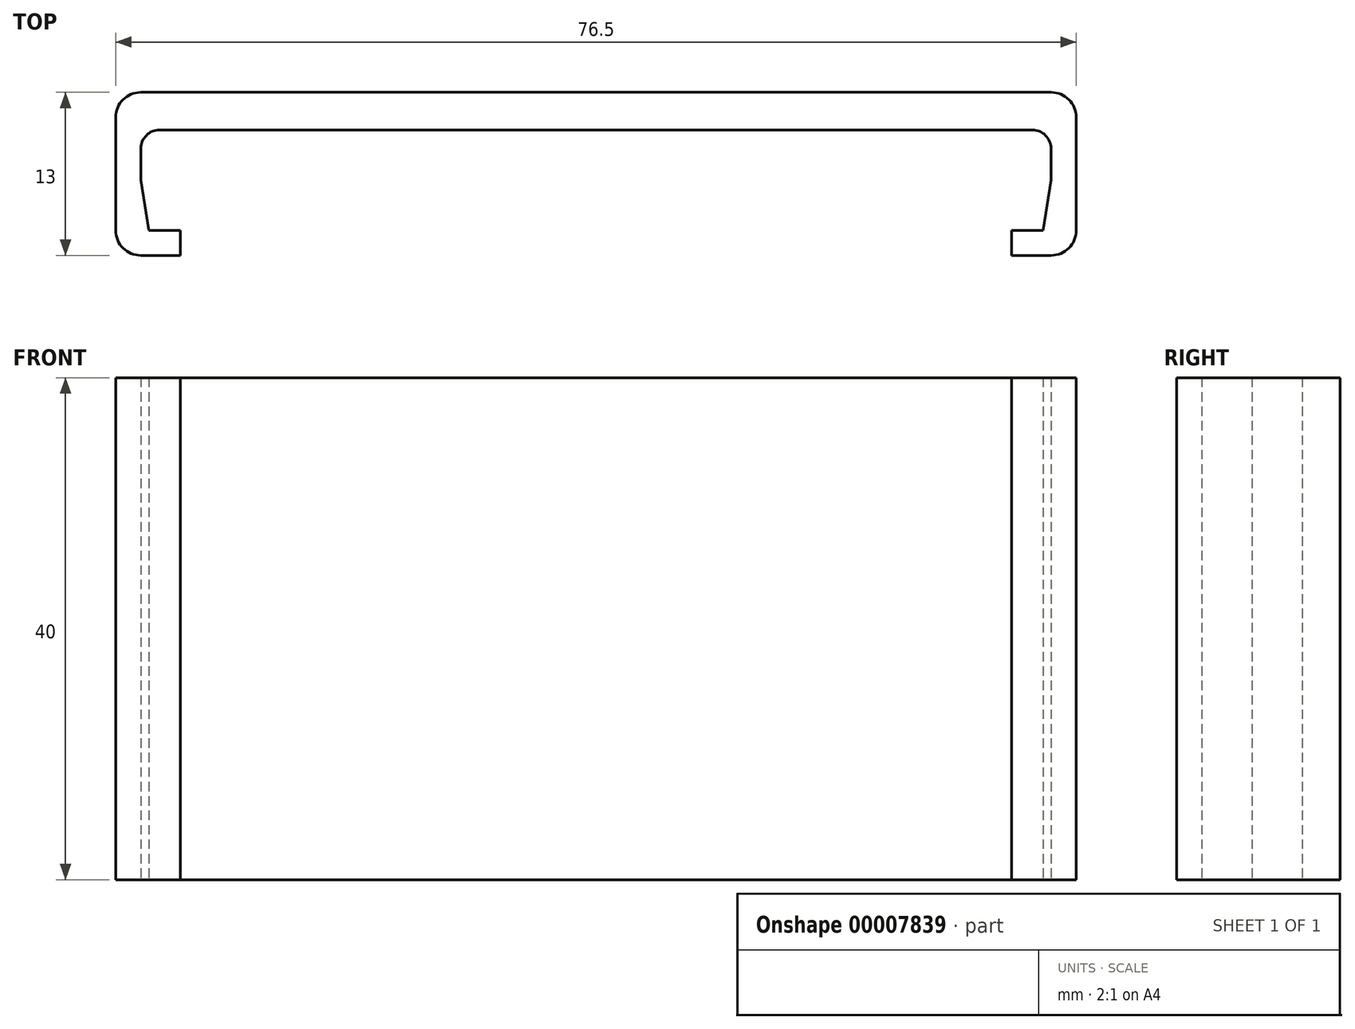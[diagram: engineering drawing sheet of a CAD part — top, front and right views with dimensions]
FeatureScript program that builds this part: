
annotation { "Feature Type Name" : "Feature", "Feature Type Description" : "" }
export const myFeature = defineFeature(function(context is Context, id is Id, definition is map)
    precondition{}
    {
        {
            var Q0;
            Q0=qCreatedBy(makeId("Top.planeOp"),FACE);
            var sketch = newSketch(context, id + "F0", { "sketchPlane" : qUnion([Q0])});
            skLineSegment(sketch, "E0", {"start": v(0, -5) * mm, "end": v(36.25, -5) * mm});
            skLineSegment(sketch, "E1", {"start": v(36.25, -5) * mm, "end": v(36.25, -9) * mm});
            skLineSegment(sketch, "E2", {"start": v(36.25, -9) * mm, "end": v(35.6, -13) * mm});
            skLineSegment(sketch, "E3", {"start": v(35.6, -13) * mm, "end": v(33.1, -13) * mm});
            skLineSegment(sketch, "E4", {"start": v(33.1, -13) * mm, "end": v(33.1, -15) * mm});
            skLineSegment(sketch, "E5", {"start": v(33.1, -15) * mm, "end": v(38.25, -15) * mm});
            skLineSegment(sketch, "E6", {"start": v(38.25, -15) * mm, "end": v(38.25, -2) * mm});
            skLineSegment(sketch, "E7", {"start": v(38.25, -2) * mm, "end": v(0, -2) * mm});
            skLineSegment(sketch, "E8.MirrorCS", {"start": v(-38.25, -2) * mm, "end": v(0, -2) * mm});
            skLineSegment(sketch, "E9.MirrorCS", {"start": v(-38.25, -15) * mm, "end": v(-38.25, -2) * mm});
            skLineSegment(sketch, "E10.MirrorCS", {"start": v(-33.1, -15) * mm, "end": v(-38.25, -15) * mm});
            skLineSegment(sketch, "E11.MirrorCS", {"start": v(-33.1, -13) * mm, "end": v(-33.1, -15) * mm});
            skLineSegment(sketch, "E12.MirrorCS", {"start": v(-35.6, -13) * mm, "end": v(-33.1, -13) * mm});
            skLineSegment(sketch, "E13.MirrorCS", {"start": v(-36.25, -9) * mm, "end": v(-35.6, -13) * mm});
            skLineSegment(sketch, "E14.MirrorCS", {"start": v(-36.25, -5) * mm, "end": v(-36.25, -9) * mm});
            skLineSegment(sketch, "E15.MirrorCS", {"start": v(0, -5) * mm, "end": v(-36.25, -5) * mm});
            skSolve(sketch);
        }
        {
            var Q0;
            Q0=makeQuery(id+"F0.imprint","IMPRINT",FACE,{"disambiguationData":[TD([[makeQuery(id+"F0.imprint","IMPRINT",EDGE,{"derivedFrom":sQuery(id+"F0.wireOp",EDGE,"E0")}),1.0]])]});
            extrude(context, id + "F1", {"entities" : qUnion([Q0]), "depth" : 40 * mm});
        }
        {
            var Q0;
            Q0=makeQuery(id+"F1.opExtrude","SWEPT_EDGE",EDGE,{"disambiguationData":[OSD([sQuery(id+"F0.wireOp",EDGE,"E5"),sQuery(id+"F0.wireOp",EDGE,"E6")])]});
            var Q1;
            Q1=makeQuery(id+"F1.opExtrude","SWEPT_EDGE",EDGE,{"disambiguationData":[OSD([sQuery(id+"F0.wireOp",EDGE,"E6"),sQuery(id+"F0.wireOp",EDGE,"E7")])]});
            var Q2;
            Q2=makeQuery(id+"F1.opExtrude","SWEPT_EDGE",EDGE,{"disambiguationData":[OSD([sQuery(id+"F0.wireOp",EDGE,"E9.MirrorCS"),sQuery(id+"F0.wireOp",EDGE,"E10.MirrorCS")])]});
            var Q3;
            Q3=makeQuery(id+"F1.opExtrude","SWEPT_EDGE",EDGE,{"disambiguationData":[OSD([sQuery(id+"F0.wireOp",EDGE,"E8.MirrorCS"),sQuery(id+"F0.wireOp",EDGE,"E9.MirrorCS")])]});
            fillet(context, id + "F2", {"entities" : qUnion([Q0, Q1, Q2, Q3]), "radius" : 2 * mm, "tangentPropagation" : true, "allowEdgeOverflow" : false});
        }
        {
            var Q0;
            Q0=makeQuery(id+"F1.opExtrude","SWEPT_EDGE",EDGE,{"disambiguationData":[OSD([sQuery(id+"F0.wireOp",EDGE,"E14.MirrorCS"),sQuery(id+"F0.wireOp",EDGE,"E15.MirrorCS")])]});
            var Q1;
            Q1=makeQuery(id+"F1.opExtrude","SWEPT_EDGE",EDGE,{"disambiguationData":[OSD([sQuery(id+"F0.wireOp",EDGE,"E0"),sQuery(id+"F0.wireOp",EDGE,"E1")])]});
            fillet(context, id + "F3", {"entities" : qUnion([Q0, Q1]), "radius" : 1.5 * mm, "tangentPropagation" : true, "allowEdgeOverflow" : false});
        }
    });
